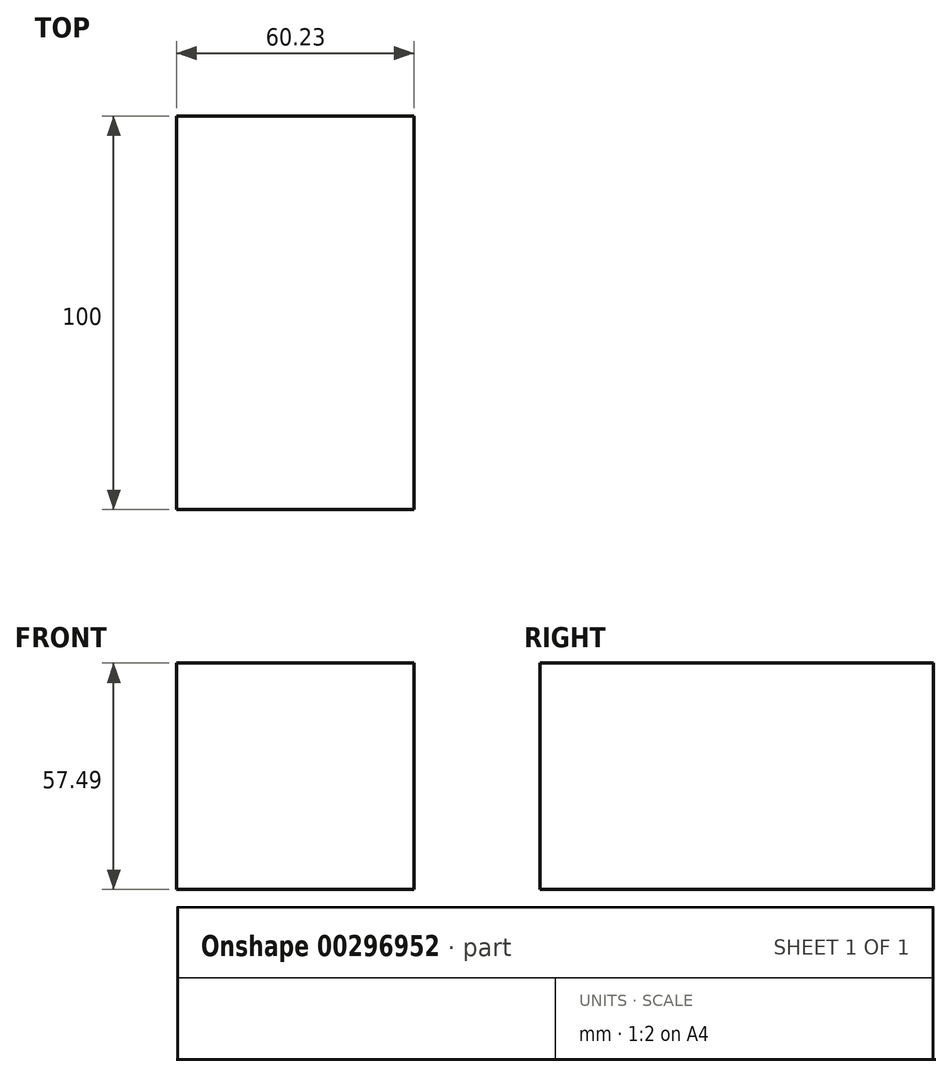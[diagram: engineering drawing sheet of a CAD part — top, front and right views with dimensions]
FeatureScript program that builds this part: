
annotation { "Feature Type Name" : "Feature", "Feature Type Description" : "" }
export const myFeature = defineFeature(function(context is Context, id is Id, definition is map)
    precondition{}
    {
        {
            var Q0;
            Q0=qCreatedBy(makeId("Front.planeOp"),FACE);
            var sketch = newSketch(context, id + "F0", { "sketchPlane" : qUnion([Q0])});
            skLineSegment(sketch, "E0.bottom", {"start": v(0, 0) * mm, "end": v(60.23, 0) * mm});
            skLineSegment(sketch, "E0.top", {"start": v(0, 57.5) * mm, "end": v(60.23, 57.5) * mm});
            skLineSegment(sketch, "E0.left", {"start": v(0, 0) * mm, "end": v(0, 57.5) * mm});
            skLineSegment(sketch, "E0.right", {"start": v(60.23, 0) * mm, "end": v(60.23, 57.5) * mm});
            skSolve(sketch);
        }
        {
            var Q0;
            Q0=makeQuery(id+"F0.imprint","IMPRINT",FACE,{"disambiguationData":[TD([[makeQuery(id+"F0.imprint","IMPRINT",EDGE,{"derivedFrom":sQuery(id+"F0.wireOp",EDGE,"E0.bottom")}),1.0]])]});
            extrude(context, id + "F1", {"entities" : qUnion([Q0]), "depth" : 100 * mm});
        }
        {
            var Q0;
            Q0=makeQuery(id+"F1.opExtrude","CAP_FACE",FACE,{"disambiguationData":[OSD([sQuery(id+"F0.wireOp",EDGE,"E0.bottom"),sQuery(id+"F0.wireOp",EDGE,"E0.top"),sQuery(id+"F0.wireOp",EDGE,"E0.left"),sQuery(id+"F0.wireOp",EDGE,"E0.right")])],"isStart":false});
            var sketch = newSketch(context, id + "F2", { "sketchPlane" : qUnion([Q0])});
            skCircle(sketch, "E1", {"center": v(21.13, 40.2) * mm, "radius": 15.75 * mm});
            skSolve(sketch);
        }
        {
            var Q0;
            Q0=sQuery(id+"F2.wireOp",EDGE,"E1");
            extrude(context, id + "F3", {"bodyType" : ToolBodyType.SURFACE, "surfaceEntities" : qUnion([Q0]), "depth" : 25 * mm});
        }
    });
